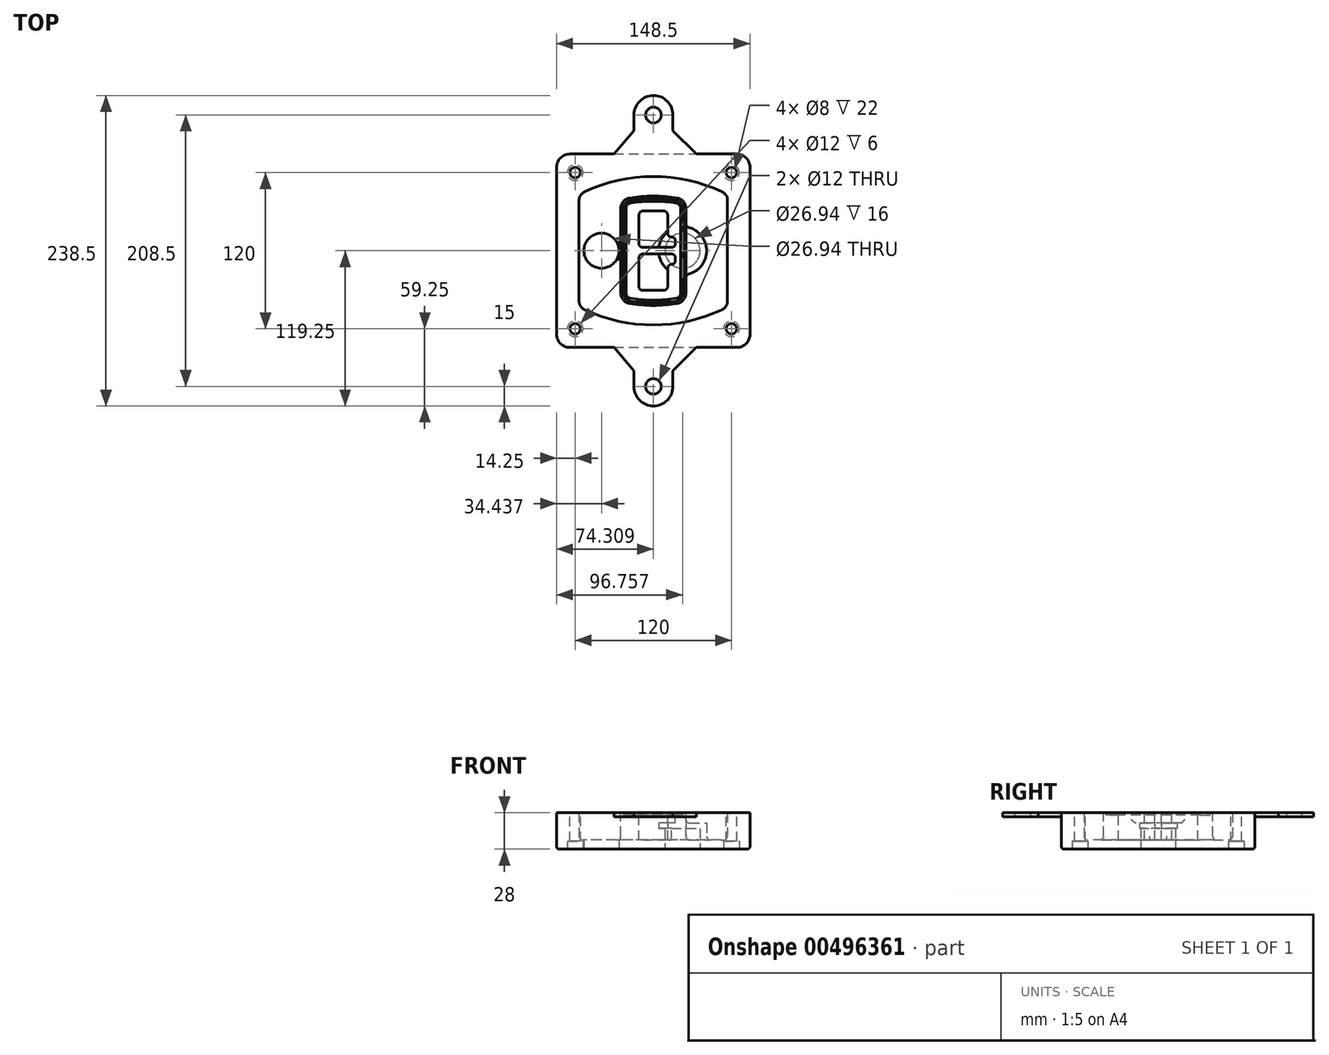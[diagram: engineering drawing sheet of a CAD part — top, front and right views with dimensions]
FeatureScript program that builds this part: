
annotation { "Feature Type Name" : "Feature", "Feature Type Description" : "" }
export const myFeature = defineFeature(function(context is Context, id is Id, definition is map)
    precondition{}
    {
        {
            var Q0;
            Q0=qCreatedBy(makeId("Top.planeOp"),FACE);
            var sketch = newSketch(context, id + "F0", { "sketchPlane" : qUnion([Q0])});
            skPoint(sketch, "E0.rect.middle", {"position": v(0, 0) * mm});
            skLineSegment(sketch, "E1.bottom", {"start": v(-64.25, -74.25) * mm, "end": v(64.25, -74.25) * mm});
            skLineSegment(sketch, "E1.top", {"start": v(-64.25, 74.25) * mm, "end": v(64.25, 74.25) * mm});
            skLineSegment(sketch, "E1.left", {"start": v(-74.25, -64.25) * mm, "end": v(-74.25, 64.25) * mm});
            skLineSegment(sketch, "E1.right", {"start": v(74.25, -64.25) * mm, "end": v(74.25, 64.25) * mm});
            skLineSegment(sketch, "E2", {"start": v(-74.25, 74.25) * mm, "end": v(74.25, -74.25) * mm, "construction": true});
            skLineSegment(sketch, "E3", {"start": v(74.25, 74.25) * mm, "end": v(-74.25, -74.25) * mm, "construction": true});
            skCircle(sketch, "E4", {"center": v(-60, 60) * mm, "radius": 4 * mm});
            skCircle(sketch, "E5", {"center": v(60, 60) * mm, "radius": 4 * mm});
            skCircle(sketch, "E6", {"center": v(60, -60) * mm, "radius": 4 * mm});
            skCircle(sketch, "E7", {"center": v(-60, -60) * mm, "radius": 4 * mm});
            skLineSegment(sketch, "E8", {"start": v(-60, 60) * mm, "end": v(60, 60) * mm, "construction": true});
            skLineSegment(sketch, "E9", {"start": v(60, 60) * mm, "end": v(60, -60) * mm, "construction": true});
            skLineSegment(sketch, "E10", {"start": v(60, -60) * mm, "end": v(-60, -60) * mm, "construction": true});
            skLineSegment(sketch, "E11", {"start": v(-60, -60) * mm, "end": v(-60, 60) * mm, "construction": true});
            skLineSegment(sketch, "E12", {"start": v(-60, 38.83) * mm, "end": v(-60, -38.83) * mm});
            skLineSegment(sketch, "E13", {"start": v(60, 38.83) * mm, "end": v(60, -38.83) * mm});
            skArc(sketch, "E14", {"start": v(54.26, 47.88) * mm, "mid": v(0, 60) * mm, "end": v(-54.26, 47.88) * mm});
            skArc(sketch, "E15", {"start": v(-54.26, -47.88) * mm, "mid": v(0, -60) * mm, "end": v(54.26, -47.88) * mm});
            skLineSegment(sketch, "E16", {"start": v(-60, 0) * mm, "end": v(60, 0) * mm, "construction": true});
            skPoint(sketch, "E17.visualSharp", {"position": v(-60, -45) * mm});
            skArc(sketch, "E17.filletArc", {"start": v(-60, -38.83) * mm, "mid": v(-58.44, -44.2) * mm, "end": v(-54.26, -47.88) * mm});
            skPoint(sketch, "E18.visualSharp", {"position": v(-60, 45) * mm});
            skArc(sketch, "E18.filletArc", {"start": v(-54.26, 47.88) * mm, "mid": v(-58.44, 44.2) * mm, "end": v(-60, 38.83) * mm});
            skPoint(sketch, "E19.visualSharp", {"position": v(60, 45) * mm});
            skArc(sketch, "E19.filletArc", {"start": v(60, 38.83) * mm, "mid": v(58.44, 44.2) * mm, "end": v(54.26, 47.88) * mm});
            skPoint(sketch, "E20.visualSharp", {"position": v(60, -45) * mm});
            skArc(sketch, "E20.filletArc", {"start": v(54.26, -47.88) * mm, "mid": v(58.44, -44.2) * mm, "end": v(60, -38.83) * mm});
            skPoint(sketch, "E21.visualSharp", {"position": v(-74.25, 74.25) * mm});
            skArc(sketch, "E21.filletArc", {"start": v(-64.25, 74.25) * mm, "mid": v(-71.32, 71.32) * mm, "end": v(-74.25, 64.25) * mm});
            skPoint(sketch, "E22.visualSharp", {"position": v(74.25, 74.25) * mm});
            skArc(sketch, "E22.filletArc", {"start": v(74.25, 64.25) * mm, "mid": v(71.32, 71.32) * mm, "end": v(64.25, 74.25) * mm});
            skPoint(sketch, "E23.visualSharp", {"position": v(74.25, -74.25) * mm});
            skArc(sketch, "E23.filletArc", {"start": v(64.25, -74.25) * mm, "mid": v(71.32, -71.32) * mm, "end": v(74.25, -64.25) * mm});
            skPoint(sketch, "E24.visualSharp", {"position": v(-74.25, -74.25) * mm});
            skArc(sketch, "E24.filletArc", {"start": v(-74.25, -64.25) * mm, "mid": v(-71.32, -71.32) * mm, "end": v(-64.25, -74.25) * mm});
            skArc(sketch, "E25.0", {"start": v(57, 38.83) * mm, "mid": v(55.9, 42.58) * mm, "end": v(52.98, 45.17) * mm});
            skLineSegment(sketch, "E25.1", {"start": v(57, 38.83) * mm, "end": v(57, -38.83) * mm});
            skArc(sketch, "E25.2", {"start": v(52.98, -45.17) * mm, "mid": v(55.9, -42.58) * mm, "end": v(57, -38.83) * mm});
            skArc(sketch, "E25.3", {"start": v(-52.98, -45.17) * mm, "mid": v(0, -57) * mm, "end": v(52.98, -45.17) * mm});
            skArc(sketch, "E25.4", {"start": v(-57, -38.83) * mm, "mid": v(-55.9, -42.58) * mm, "end": v(-52.98, -45.17) * mm});
            skArc(sketch, "E25.5", {"start": v(52.98, 45.17) * mm, "mid": v(0, 57) * mm, "end": v(-52.98, 45.17) * mm});
            skLineSegment(sketch, "E25.6", {"start": v(-57, 38.83) * mm, "end": v(-57, -38.83) * mm});
            skArc(sketch, "E25.7", {"start": v(-52.98, 45.17) * mm, "mid": v(-55.9, 42.58) * mm, "end": v(-57, 38.83) * mm});
            skArc(sketch, "E26.0", {"start": v(-55.96, 51.5) * mm, "mid": v(-61.82, 46.33) * mm, "end": v(-64, 38.83) * mm});
            skArc(sketch, "E26.1", {"start": v(55.96, 51.5) * mm, "mid": v(0, 64) * mm, "end": v(-55.96, 51.5) * mm});
            skArc(sketch, "E26.2", {"start": v(64, 38.83) * mm, "mid": v(61.82, 46.33) * mm, "end": v(55.96, 51.5) * mm});
            skLineSegment(sketch, "E26.3", {"start": v(64, 38.83) * mm, "end": v(64, -38.83) * mm});
            skArc(sketch, "E26.4", {"start": v(55.96, -51.5) * mm, "mid": v(61.82, -46.33) * mm, "end": v(64, -38.83) * mm});
            skLineSegment(sketch, "E26.5", {"start": v(-64, 38.83) * mm, "end": v(-64, -38.83) * mm});
            skArc(sketch, "E26.6", {"start": v(-55.96, -51.5) * mm, "mid": v(0, -64) * mm, "end": v(55.96, -51.5) * mm});
            skArc(sketch, "E26.7", {"start": v(-64, -38.83) * mm, "mid": v(-61.82, -46.33) * mm, "end": v(-55.96, -51.5) * mm});
            skSolve(sketch);
        }
        {
            var Q0;
            Q0=makeQuery(id+"F0.imprint","IMPRINT",FACE,{"disambiguationData":[TD([[makeQuery(id+"F0.imprint","IMPRINT",EDGE,{"derivedFrom":sQuery(id+"F0.wireOp",EDGE,"E1.bottom")}),1.0]])]});
            var Q1;
            Q1=makeQuery(id+"F0.imprint","IMPRINT",FACE,{"disambiguationData":[TD([[makeQuery(id+"F0.imprint","IMPRINT",EDGE,{"derivedFrom":sQuery(id+"F0.wireOp",EDGE,"E12")}),1.0]])]});
            var Q2;
            Q2=makeQuery(id+"F0.imprint","IMPRINT",FACE,{"disambiguationData":[TD([[makeQuery(id+"F0.imprint","IMPRINT",EDGE,{"derivedFrom":sQuery(id+"F0.wireOp",EDGE,"E25.0")}),1.0]])]});
            var Q3;
            Q3=makeQuery(id+"F0.imprint","IMPRINT",FACE,{"disambiguationData":[TD([[makeQuery(id+"F0.imprint","IMPRINT",EDGE,{"derivedFrom":sQuery(id+"F0.wireOp",EDGE,"E12")}),-1.0]])]});
            extrude(context, id + "F1", {"entities" : qUnion([Q0, Q1, Q2, Q3]), "oppositeDirection" : true, "depth" : 25 * mm});
        }
        {
            var Q0;
            Q0=makeQuery(id+"F0.imprint","IMPRINT",FACE,{"disambiguationData":[TD([[makeQuery(id+"F0.imprint","IMPRINT",EDGE,{"derivedFrom":sQuery(id+"F0.wireOp",EDGE,"E12")}),1.0]])]});
            extrude(context, id + "F2", {"entities" : qUnion([Q0]), "operationType" : NewBodyOperationType.ADD, "depth" : 3 * mm});
        }
        {
            var Q0;
            Q0=makeQuery(id+"F0.imprint","IMPRINT",FACE,{"disambiguationData":[TD([[makeQuery(id+"F0.imprint","IMPRINT",EDGE,{"derivedFrom":sQuery(id+"F0.wireOp",EDGE,"E25.0")}),1.0]])]});
            extrude(context, id + "F3", {"entities" : qUnion([Q0]), "operationType" : NewBodyOperationType.REMOVE, "oppositeDirection" : true, "depth" : 18 * mm});
        }
        {
            var Q0;
            Q0=makeQuery(id+"F2.opExtrude","CAP_FACE",FACE,{"disambiguationData":[OSD([sQuery(id+"F0.wireOp",EDGE,"E12"),sQuery(id+"F0.wireOp",EDGE,"E13"),sQuery(id+"F0.wireOp",EDGE,"E14"),sQuery(id+"F0.wireOp",EDGE,"E15"),sQuery(id+"F0.wireOp",EDGE,"E17.filletArc"),sQuery(id+"F0.wireOp",EDGE,"E18.filletArc"),sQuery(id+"F0.wireOp",EDGE,"E19.filletArc"),sQuery(id+"F0.wireOp",EDGE,"E20.filletArc"),sQuery(id+"F0.wireOp",EDGE,"E25.0"),sQuery(id+"F0.wireOp",EDGE,"E25.1"),sQuery(id+"F0.wireOp",EDGE,"E25.2"),sQuery(id+"F0.wireOp",EDGE,"E25.3"),sQuery(id+"F0.wireOp",EDGE,"E25.4"),sQuery(id+"F0.wireOp",EDGE,"E25.5"),sQuery(id+"F0.wireOp",EDGE,"E25.6"),sQuery(id+"F0.wireOp",EDGE,"E25.7")])],"isStart":false});
            var sketch = newSketch(context, id + "F4", { "sketchPlane" : qUnion([Q0])});
            skArc(sketch, "E27.0", {"start": v(-18.34, -40.45) * mm, "mid": v(0, -42) * mm, "end": v(18.34, -40.45) * mm});
            skArc(sketch, "E28.0", {"start": v(18.34, 40.45) * mm, "mid": v(0, 42) * mm, "end": v(-18.34, 40.45) * mm});
            skLineSegment(sketch, "E29", {"start": v(-25, 32.57) * mm, "end": v(-25, -32.57) * mm});
            skLineSegment(sketch, "E30", {"start": v(25, 32.57) * mm, "end": v(25, -32.57) * mm});
            skLineSegment(sketch, "E31", {"start": v(-25, 39.1) * mm, "end": v(25, 39.1) * mm, "construction": true});
            skLineSegment(sketch, "E32", {"start": v(-25, -39.1) * mm, "end": v(25, -39.1) * mm, "construction": true});
            skPoint(sketch, "E33.visualSharp", {"position": v(-25, 39.1) * mm});
            skArc(sketch, "E33.filletArc", {"start": v(-18.34, 40.45) * mm, "mid": v(-23.11, 37.73) * mm, "end": v(-25, 32.57) * mm});
            skPoint(sketch, "E34.visualSharp", {"position": v(25, 39.1) * mm});
            skArc(sketch, "E34.filletArc", {"start": v(25, 32.57) * mm, "mid": v(23.11, 37.73) * mm, "end": v(18.34, 40.45) * mm});
            skPoint(sketch, "E35.visualSharp", {"position": v(25, -39.1) * mm});
            skArc(sketch, "E35.filletArc", {"start": v(18.34, -40.45) * mm, "mid": v(23.11, -37.73) * mm, "end": v(25, -32.57) * mm});
            skPoint(sketch, "E36.visualSharp", {"position": v(-25, -39.1) * mm});
            skArc(sketch, "E36.filletArc", {"start": v(-25, -32.57) * mm, "mid": v(-23.11, -37.73) * mm, "end": v(-18.34, -40.45) * mm});
            skArc(sketch, "E37.0", {"start": v(52.98, 45.17) * mm, "mid": v(0, 57) * mm, "end": v(-52.98, 45.17) * mm});
            skArc(sketch, "E37.1", {"start": v(-52.98, 45.17) * mm, "mid": v(-55.9, 42.58) * mm, "end": v(-57, 38.83) * mm});
            skLineSegment(sketch, "E37.2", {"start": v(-57, 38.83) * mm, "end": v(-57, -38.83) * mm});
            skArc(sketch, "E37.3", {"start": v(-57, -38.83) * mm, "mid": v(-55.9, -42.58) * mm, "end": v(-52.98, -45.17) * mm});
            skArc(sketch, "E37.4", {"start": v(-52.98, -45.17) * mm, "mid": v(0, -57) * mm, "end": v(52.98, -45.17) * mm});
            skArc(sketch, "E37.5", {"start": v(52.98, -45.17) * mm, "mid": v(55.9, -42.58) * mm, "end": v(57, -38.83) * mm});
            skLineSegment(sketch, "E37.6", {"start": v(57, 38.83) * mm, "end": v(57, -38.83) * mm});
            skArc(sketch, "E37.7", {"start": v(57, 38.83) * mm, "mid": v(55.9, 42.58) * mm, "end": v(52.98, 45.17) * mm});
            skLineSegment(sketch, "E38.0", {"start": v(23, 32.57) * mm, "end": v(23, -32.57) * mm});
            skArc(sketch, "E38.1", {"start": v(18, -38.48) * mm, "mid": v(21.58, -36.44) * mm, "end": v(23, -32.57) * mm});
            skArc(sketch, "E38.2", {"start": v(-18, -38.48) * mm, "mid": v(0, -40) * mm, "end": v(18, -38.48) * mm});
            skArc(sketch, "E38.3", {"start": v(-23, -32.57) * mm, "mid": v(-21.58, -36.44) * mm, "end": v(-18, -38.48) * mm});
            skLineSegment(sketch, "E38.4", {"start": v(-23, 32.57) * mm, "end": v(-23, -32.57) * mm});
            skArc(sketch, "E38.5", {"start": v(23, 32.57) * mm, "mid": v(21.58, 36.44) * mm, "end": v(18, 38.48) * mm});
            skArc(sketch, "E38.6", {"start": v(-18, 38.48) * mm, "mid": v(-21.58, 36.44) * mm, "end": v(-23, 32.57) * mm});
            skArc(sketch, "E38.7", {"start": v(18, 38.48) * mm, "mid": v(0, 40) * mm, "end": v(-18, 38.48) * mm});
            skArc(sketch, "E39.0", {"start": v(21, 32.57) * mm, "mid": v(20.06, 35.15) * mm, "end": v(17.67, 36.5) * mm});
            skLineSegment(sketch, "E39.1", {"start": v(21, 32.57) * mm, "end": v(21, -32.57) * mm});
            skArc(sketch, "E39.2", {"start": v(17.67, -36.5) * mm, "mid": v(20.06, -35.15) * mm, "end": v(21, -32.57) * mm});
            skArc(sketch, "E39.3", {"start": v(-17.67, -36.5) * mm, "mid": v(0, -38) * mm, "end": v(17.67, -36.5) * mm});
            skArc(sketch, "E39.4", {"start": v(-21, -32.57) * mm, "mid": v(-20.06, -35.15) * mm, "end": v(-17.67, -36.5) * mm});
            skArc(sketch, "E39.5", {"start": v(17.67, 36.5) * mm, "mid": v(0, 38) * mm, "end": v(-17.67, 36.5) * mm});
            skLineSegment(sketch, "E39.6", {"start": v(-21, 32.57) * mm, "end": v(-21, -32.57) * mm});
            skArc(sketch, "E39.7", {"start": v(-17.67, 36.5) * mm, "mid": v(-20.06, 35.15) * mm, "end": v(-21, 32.57) * mm});
            skLineSegment(sketch, "E40", {"start": v(-25, 0) * mm, "end": v(25, 0) * mm, "construction": true});
            skLineSegment(sketch, "E41", {"start": v(-11, 5.5) * mm, "end": v(-11, 27.5) * mm});
            skLineSegment(sketch, "E42", {"start": v(-8, 30.5) * mm, "end": v(8, 30.5) * mm});
            skLineSegment(sketch, "E43", {"start": v(11, 27.5) * mm, "end": v(11, 13.5) * mm});
            skLineSegment(sketch, "E44", {"start": v(14, 10.5) * mm, "end": v(14, 10.5) * mm});
            skLineSegment(sketch, "E45", {"start": v(17, 7.5) * mm, "end": v(17, 5.5) * mm});
            skLineSegment(sketch, "E46", {"start": v(14, 2.5) * mm, "end": v(-8, 2.5) * mm});
            skPoint(sketch, "E47.visualSharp", {"position": v(-11, 30.5) * mm});
            skArc(sketch, "E47.filletArc", {"start": v(-8, 30.5) * mm, "mid": v(-10.12, 29.62) * mm, "end": v(-11, 27.5) * mm});
            skPoint(sketch, "E48.visualSharp", {"position": v(11, 30.5) * mm});
            skArc(sketch, "E48.filletArc", {"start": v(11, 27.5) * mm, "mid": v(10.12, 29.62) * mm, "end": v(8, 30.5) * mm});
            skPoint(sketch, "E49.visualSharp", {"position": v(11, 10.5) * mm});
            skArc(sketch, "E49.filletArc", {"start": v(11, 13.5) * mm, "mid": v(11.88, 11.38) * mm, "end": v(14, 10.5) * mm});
            skPoint(sketch, "E50.visualSharp", {"position": v(17, 10.5) * mm});
            skArc(sketch, "E50.filletArc", {"start": v(17, 7.5) * mm, "mid": v(16.12, 9.62) * mm, "end": v(14, 10.5) * mm});
            skPoint(sketch, "E51.visualSharp", {"position": v(17, 2.5) * mm});
            skArc(sketch, "E51.filletArc", {"start": v(14, 2.5) * mm, "mid": v(16.12, 3.38) * mm, "end": v(17, 5.5) * mm});
            skPoint(sketch, "E52.visualSharp", {"position": v(-11, 2.5) * mm});
            skArc(sketch, "E52.filletArc", {"start": v(-11, 5.5) * mm, "mid": v(-10.12, 3.38) * mm, "end": v(-8, 2.5) * mm});
            skLineSegment(sketch, "E53.0.MirrorCS", {"start": v(14, -2.5) * mm, "end": v(-8, -2.5) * mm});
            skArc(sketch, "E54.0.MirrorCS", {"start": v(-11, -5.5) * mm, "mid": v(-10.12, -3.38) * mm, "end": v(-8, -2.5) * mm});
            skLineSegment(sketch, "E55.0.MirrorCS", {"start": v(-11, -5.5) * mm, "end": v(-11, -27.5) * mm});
            skArc(sketch, "E56.0.MirrorCS", {"start": v(-8, -30.5) * mm, "mid": v(-10.12, -29.62) * mm, "end": v(-11, -27.5) * mm});
            skLineSegment(sketch, "E57.0.MirrorCS", {"start": v(-8, -30.5) * mm, "end": v(8, -30.5) * mm});
            skArc(sketch, "E58.0.MirrorCS", {"start": v(11, -27.5) * mm, "mid": v(10.12, -29.62) * mm, "end": v(8, -30.5) * mm});
            skLineSegment(sketch, "E59.0.MirrorCS", {"start": v(11, -27.5) * mm, "end": v(11, -13.5) * mm});
            skArc(sketch, "E60.0.MirrorCS", {"start": v(11, -13.5) * mm, "mid": v(11.88, -11.38) * mm, "end": v(14, -10.5) * mm});
            skArc(sketch, "E61.0.MirrorCS", {"start": v(17, -7.5) * mm, "mid": v(16.12, -9.62) * mm, "end": v(14, -10.5) * mm});
            skLineSegment(sketch, "E62.0.MirrorCS", {"start": v(17, -7.5) * mm, "end": v(17, -5.5) * mm});
            skArc(sketch, "E63.0.MirrorCS", {"start": v(14, -2.5) * mm, "mid": v(16.12, -3.38) * mm, "end": v(17, -5.5) * mm});
            skSolve(sketch);
        }
        {
            var Q0;
            Q0=makeQuery(id+"F4.imprint","IMPRINT",FACE,{"disambiguationData":[TD([[makeQuery(id+"F4.imprint","IMPRINT",EDGE,{"derivedFrom":sQuery(id+"F4.wireOp",EDGE,"E27.0")}),1.0]])]});
            var Q1;
            Q1=makeQuery(id+"F4.imprint","IMPRINT",FACE,{"disambiguationData":[TD([[makeQuery(id+"F4.imprint","IMPRINT",EDGE,{"derivedFrom":sQuery(id+"F4.wireOp",EDGE,"E38.0")}),-1.0]])]});
            var Q2;
            Q2=makeQuery(id+"F4.imprint","IMPRINT",FACE,{"disambiguationData":[TD([[makeQuery(id+"F4.imprint","IMPRINT",EDGE,{"derivedFrom":sQuery(id+"F4.wireOp",EDGE,"E39.0")}),1.0]])]});
            extrude(context, id + "F5", {"entities" : qUnion([Q0, Q1, Q2]), "operationType" : NewBodyOperationType.ADD, "endBound" : BoundingType.UP_TO_NEXT, "oppositeDirection" : true, "depth" : 25 * mm});
        }
        {
            var Q0;
            Q0=makeQuery(id+"F4.imprint","IMPRINT",FACE,{"disambiguationData":[TD([[makeQuery(id+"F4.imprint","IMPRINT",EDGE,{"derivedFrom":sQuery(id+"F4.wireOp",EDGE,"E38.0")}),-1.0]])]});
            extrude(context, id + "F6", {"entities" : qUnion([Q0]), "operationType" : NewBodyOperationType.REMOVE, "oppositeDirection" : true, "depth" : 2 * mm});
        }
        {
            var Q0;
            Q0=makeQuery(id+"F1.opExtrude","CAP_FACE",FACE,{"disambiguationData":[OSD([sQuery(id+"F0.wireOp",EDGE,"E1.bottom"),sQuery(id+"F0.wireOp",EDGE,"E1.top"),sQuery(id+"F0.wireOp",EDGE,"E1.left"),sQuery(id+"F0.wireOp",EDGE,"E1.right"),sQuery(id+"F0.wireOp",EDGE,"E4"),sQuery(id+"F0.wireOp",EDGE,"E5"),sQuery(id+"F0.wireOp",EDGE,"E6"),sQuery(id+"F0.wireOp",EDGE,"E7"),sQuery(id+"F0.wireOp",EDGE,"E21.filletArc"),sQuery(id+"F0.wireOp",EDGE,"E22.filletArc"),sQuery(id+"F0.wireOp",EDGE,"E23.filletArc"),sQuery(id+"F0.wireOp",EDGE,"E24.filletArc")])],"isStart":false});
            var sketch = newSketch(context, id + "F7", { "sketchPlane" : qUnion([Q0])});
            skCircle(sketch, "E64", {"center": v(22.5, 0) * mm, "radius": 13.47 * mm});
            skCircle(sketch, "E65", {"center": v(-39.81, 0) * mm, "radius": 13.47 * mm});
            skLineSegment(sketch, "E66", {"start": v(74.25, 0) * mm, "end": v(-74.25, 0) * mm});
            skCircle(sketch, "E67", {"center": v(22.5, 0) * mm, "radius": 18.47 * mm});
            skCircle(sketch, "E68", {"center": v(60, -60) * mm, "radius": 6 * mm});
            skCircle(sketch, "E69", {"center": v(-60, -60) * mm, "radius": 6 * mm});
            skCircle(sketch, "E70", {"center": v(-60, 60) * mm, "radius": 6 * mm});
            skCircle(sketch, "E71", {"center": v(60, 60) * mm, "radius": 6 * mm});
            skSolve(sketch);
        }
        {
            var Q0;
            {var subQ1=sQuery(id+"F7.wireOp",EDGE,"E66");var subQ4=sQuery(id+"F7.wireOp",EDGE,"E64");var subQ6=makeQuery(id+"F7.imprint","INTERSECT",VERTEX,{"disambiguationData":[OD(0.0)],"derivedFrom":[subQ4,subQ1]});Q0=makeQuery(id+"F7.imprint","IMPRINT",FACE,{"disambiguationData":[TD([[makeQuery(id+"F7.imprint","IMPRINT",EDGE,{"disambiguationData":[TD([[subQ6,-1.0]])],"derivedFrom":subQ4}),-1.0]])]});}
            var Q1;
            {var subQ0=sQuery(id+"F7.wireOp",EDGE,"E66");var subQ1=sQuery(id+"F7.wireOp",EDGE,"E64");var subQ3=makeQuery(id+"F7.imprint","INTERSECT",VERTEX,{"disambiguationData":[OD(0.0)],"derivedFrom":[subQ1,subQ0]});Q1=makeQuery(id+"F7.imprint","IMPRINT",FACE,{"disambiguationData":[TD([[makeQuery(id+"F7.imprint","IMPRINT",EDGE,{"disambiguationData":[TD([[subQ3,-1.0]])],"derivedFrom":subQ1}),1.0]])]});}
            var Q2;
            {var subQ0=sQuery(id+"F7.wireOp",EDGE,"E66");var subQ1=sQuery(id+"F7.wireOp",EDGE,"E64");var subQ3=makeQuery(id+"F7.imprint","INTERSECT",VERTEX,{"disambiguationData":[OD(0.0)],"derivedFrom":[subQ1,subQ0]});Q2=makeQuery(id+"F7.imprint","IMPRINT",FACE,{"disambiguationData":[TD([[makeQuery(id+"F7.imprint","IMPRINT",EDGE,{"disambiguationData":[TD([[subQ3,1.0]])],"derivedFrom":subQ1}),1.0]])]});}
            var Q3;
            {var subQ1=sQuery(id+"F7.wireOp",EDGE,"E66");var subQ4=sQuery(id+"F7.wireOp",EDGE,"E64");var subQ6=makeQuery(id+"F7.imprint","INTERSECT",VERTEX,{"disambiguationData":[OD(0.0)],"derivedFrom":[subQ4,subQ1]});Q3=makeQuery(id+"F7.imprint","IMPRINT",FACE,{"disambiguationData":[TD([[makeQuery(id+"F7.imprint","IMPRINT",EDGE,{"disambiguationData":[TD([[subQ6,1.0]])],"derivedFrom":subQ4}),-1.0]])]});}
            extrude(context, id + "F8", {"entities" : qUnion([Q0, Q1, Q2, Q3]), "operationType" : NewBodyOperationType.ADD, "oppositeDirection" : true, "depth" : 20 * mm});
        }
        {
            var Q0;
            {var subQ0=sQuery(id+"F7.wireOp",EDGE,"E66");var subQ1=sQuery(id+"F7.wireOp",EDGE,"E64");var subQ3=makeQuery(id+"F7.imprint","INTERSECT",VERTEX,{"disambiguationData":[OD(0.0)],"derivedFrom":[subQ1,subQ0]});Q0=makeQuery(id+"F7.imprint","IMPRINT",FACE,{"disambiguationData":[TD([[makeQuery(id+"F7.imprint","IMPRINT",EDGE,{"disambiguationData":[TD([[subQ3,-1.0]])],"derivedFrom":subQ1}),1.0]])]});}
            var Q1;
            {var subQ0=sQuery(id+"F7.wireOp",EDGE,"E66");var subQ1=sQuery(id+"F7.wireOp",EDGE,"E64");var subQ3=makeQuery(id+"F7.imprint","INTERSECT",VERTEX,{"disambiguationData":[OD(0.0)],"derivedFrom":[subQ1,subQ0]});Q1=makeQuery(id+"F7.imprint","IMPRINT",FACE,{"disambiguationData":[TD([[makeQuery(id+"F7.imprint","IMPRINT",EDGE,{"disambiguationData":[TD([[subQ3,1.0]])],"derivedFrom":subQ1}),1.0]])]});}
            extrude(context, id + "F9", {"entities" : qUnion([Q0, Q1]), "operationType" : NewBodyOperationType.REMOVE, "oppositeDirection" : true, "depth" : 16 * mm});
        }
        {
            var Q0;
            {var subQ0=sQuery(id+"F7.wireOp",EDGE,"E66");var subQ1=sQuery(id+"F7.wireOp",EDGE,"E65");var subQ3=makeQuery(id+"F7.imprint","INTERSECT",VERTEX,{"disambiguationData":[OD(0.0)],"derivedFrom":[subQ1,subQ0]});Q0=makeQuery(id+"F7.imprint","IMPRINT",FACE,{"disambiguationData":[TD([[makeQuery(id+"F7.imprint","IMPRINT",EDGE,{"disambiguationData":[TD([[subQ3,-1.0]])],"derivedFrom":subQ1}),1.0]])]});}
            var Q1;
            {var subQ0=sQuery(id+"F7.wireOp",EDGE,"E66");var subQ1=sQuery(id+"F7.wireOp",EDGE,"E65");var subQ3=makeQuery(id+"F7.imprint","INTERSECT",VERTEX,{"disambiguationData":[OD(0.0)],"derivedFrom":[subQ1,subQ0]});Q1=makeQuery(id+"F7.imprint","IMPRINT",FACE,{"disambiguationData":[TD([[makeQuery(id+"F7.imprint","IMPRINT",EDGE,{"disambiguationData":[TD([[subQ3,1.0]])],"derivedFrom":subQ1}),1.0]])]});}
            extrude(context, id + "F10", {"entities" : qUnion([Q0, Q1]), "operationType" : NewBodyOperationType.REMOVE, "oppositeDirection" : true, "depth" : 25 * mm});
        }
        {
            var Q0;
            Q0=makeQuery(id+"F7.imprint","IMPRINT",FACE,{"disambiguationData":[TD([[makeQuery(id+"F7.imprint","IMPRINT",EDGE,{"derivedFrom":sQuery(id+"F7.wireOp",EDGE,"E68")}),1.0]])]});
            var Q1;
            Q1=makeQuery(id+"F7.imprint","IMPRINT",FACE,{"disambiguationData":[TD([[makeQuery(id+"F7.imprint","IMPRINT",EDGE,{"derivedFrom":makeQuery(id+"F1.opExtrude","CAP_EDGE",EDGE,{"disambiguationData":[OSD([sQuery(id+"F0.wireOp",EDGE,"E5")])],"isStart":false})}),-1.0]])]});
            var Q2;
            Q2=makeQuery(id+"F7.imprint","IMPRINT",FACE,{"disambiguationData":[TD([[makeQuery(id+"F7.imprint","IMPRINT",EDGE,{"derivedFrom":sQuery(id+"F7.wireOp",EDGE,"E69")}),1.0]])]});
            var Q3;
            Q3=makeQuery(id+"F7.imprint","IMPRINT",FACE,{"disambiguationData":[TD([[makeQuery(id+"F7.imprint","IMPRINT",EDGE,{"derivedFrom":makeQuery(id+"F1.opExtrude","CAP_EDGE",EDGE,{"disambiguationData":[OSD([sQuery(id+"F0.wireOp",EDGE,"E4")])],"isStart":false})}),-1.0]])]});
            var Q4;
            Q4=makeQuery(id+"F7.imprint","IMPRINT",FACE,{"disambiguationData":[TD([[makeQuery(id+"F7.imprint","IMPRINT",EDGE,{"derivedFrom":sQuery(id+"F7.wireOp",EDGE,"E70")}),1.0]])]});
            var Q5;
            Q5=makeQuery(id+"F7.imprint","IMPRINT",FACE,{"disambiguationData":[TD([[makeQuery(id+"F7.imprint","IMPRINT",EDGE,{"derivedFrom":makeQuery(id+"F1.opExtrude","CAP_EDGE",EDGE,{"disambiguationData":[OSD([sQuery(id+"F0.wireOp",EDGE,"E7")])],"isStart":false})}),-1.0]])]});
            var Q6;
            Q6=makeQuery(id+"F7.imprint","IMPRINT",FACE,{"disambiguationData":[TD([[makeQuery(id+"F7.imprint","IMPRINT",EDGE,{"derivedFrom":sQuery(id+"F7.wireOp",EDGE,"E71")}),1.0]])]});
            var Q7;
            Q7=makeQuery(id+"F7.imprint","IMPRINT",FACE,{"disambiguationData":[TD([[makeQuery(id+"F7.imprint","IMPRINT",EDGE,{"derivedFrom":makeQuery(id+"F1.opExtrude","CAP_EDGE",EDGE,{"disambiguationData":[OSD([sQuery(id+"F0.wireOp",EDGE,"E6")])],"isStart":false})}),-1.0]])]});
            extrude(context, id + "F11", {"entities" : qUnion([Q0, Q1, Q2, Q3, Q4, Q5, Q6, Q7]), "operationType" : NewBodyOperationType.REMOVE, "oppositeDirection" : true, "depth" : 6 * mm});
        }
        {
            var Q0;
            Q0=makeQuery(id+"F9.boolean.opBoolean","COPY",FACE,{"derivedFrom":makeQuery(id+"F9.opExtrude","CAP_FACE",FACE,{"disambiguationData":[OSD([sQuery(id+"F7.wireOp",EDGE,"E64")])],"isStart":false})});
            var sketch = newSketch(context, id + "F12", { "sketchPlane" : qUnion([Q0])});
            skArc(sketch, "E72.0", {"start": v(11, 14.45) * mm, "mid": v(6.45, 9.13) * mm, "end": v(4.2, 2.5) * mm});
            skArc(sketch, "E72.1", {"start": v(4.2, -2.5) * mm, "mid": v(6.45, -9.13) * mm, "end": v(11, -14.45) * mm});
            skLineSegment(sketch, "E73", {"start": v(4.2, -2.5) * mm, "end": v(14, -2.5) * mm});
            skLineSegment(sketch, "E74.0", {"start": v(14, 2.5) * mm, "end": v(4.2, 2.5) * mm});
            skArc(sketch, "E74.1", {"start": v(14, 2.5) * mm, "mid": v(16.12, 3.38) * mm, "end": v(17, 5.5) * mm});
            skLineSegment(sketch, "E74.2", {"start": v(17, 7.5) * mm, "end": v(17, 5.5) * mm});
            skArc(sketch, "E74.3", {"start": v(17, 7.5) * mm, "mid": v(16.12, 9.62) * mm, "end": v(14, 10.5) * mm});
            skArc(sketch, "E74.4", {"start": v(11, 13.5) * mm, "mid": v(11.88, 11.38) * mm, "end": v(14, 10.5) * mm});
            skLineSegment(sketch, "E74.5", {"start": v(11, 14.45) * mm, "end": v(11, 13.5) * mm});
            skLineSegment(sketch, "E74.7", {"start": v(14, -2.5) * mm, "end": v(4.2, -2.5) * mm});
            skArc(sketch, "E74.8", {"start": v(14, -2.5) * mm, "mid": v(16.12, -3.38) * mm, "end": v(17, -5.5) * mm});
            skLineSegment(sketch, "E74.9", {"start": v(17, -7.5) * mm, "end": v(17, -5.5) * mm});
            skArc(sketch, "E74.10", {"start": v(17, -7.5) * mm, "mid": v(16.12, -9.62) * mm, "end": v(14, -10.5) * mm});
            skArc(sketch, "E74.11", {"start": v(11, -13.5) * mm, "mid": v(11.88, -11.38) * mm, "end": v(14, -10.5) * mm});
            skLineSegment(sketch, "E74.12", {"start": v(11, -14.45) * mm, "end": v(11, -13.5) * mm});
            skPoint(sketch, "E75.orphan", {"position": v(11, -27.5) * mm});
            skPoint(sketch, "E76.orphan", {"position": v(-8, -2.5) * mm});
            skPoint(sketch, "E77.orphan", {"position": v(-8, 2.5) * mm});
            skPoint(sketch, "E78.orphan", {"position": v(11, 27.5) * mm});
            skSolve(sketch);
        }
        {
            var Q0;
            {var subQ7=sQuery(id+"F12.wireOp",EDGE,"E72.0");var subQ14=sQuery(id+"F12.wireOp",EDGE,"E72.1");var subQ16=sQuery(id+"F12.wireOp",EDGE,"E74.1");var subQ18=sQuery(id+"F12.wireOp",EDGE,"E74.8");Q0=qUnion([makeQuery(id+"F12.imprint","IMPRINT",FACE,{"disambiguationData":[TD([[makeQuery(id+"F12.imprint","IMPRINT",EDGE,{"derivedFrom":subQ7}),1.0]])]}),makeQuery(id+"F12.imprint","IMPRINT",FACE,{"disambiguationData":[TD([[makeQuery(id+"F12.imprint","IMPRINT",EDGE,{"derivedFrom":subQ14}),1.0]])]}),makeQuery(id+"F12.imprint","IMPRINT",FACE,{"disambiguationData":[TD([[makeQuery(id+"F12.imprint","IMPRINT",EDGE,{"derivedFrom":subQ16}),1.0]])]}),makeQuery(id+"F12.imprint","IMPRINT",FACE,{"disambiguationData":[TD([[makeQuery(id+"F12.imprint","IMPRINT",EDGE,{"derivedFrom":subQ18}),-1.0]])]})]);}
            var Q1;
            Q1=makeQuery(id+"F5.boolean.opBoolean","SPLIT",FACE,{"disambiguationData":[TD([makeQuery(id+"F5.opExtrude","SWEPT_FACE",FACE,{"disambiguationData":[OSD([sQuery(id+"F4.wireOp",EDGE,"E41")])]})])],"derivedFrom":makeQuery(id+"F3.boolean.opBoolean","COPY",FACE,{"derivedFrom":makeQuery(id+"F3.opExtrude","CAP_FACE",FACE,{"disambiguationData":[OSD([sQuery(id+"F0.wireOp",EDGE,"E25.0"),sQuery(id+"F0.wireOp",EDGE,"E25.1"),sQuery(id+"F0.wireOp",EDGE,"E25.2"),sQuery(id+"F0.wireOp",EDGE,"E25.3"),sQuery(id+"F0.wireOp",EDGE,"E25.4"),sQuery(id+"F0.wireOp",EDGE,"E25.5"),sQuery(id+"F0.wireOp",EDGE,"E25.6"),sQuery(id+"F0.wireOp",EDGE,"E25.7")])],"isStart":false})})});
            extrude(context, id + "F13", {"entities" : qUnion([Q0]), "operationType" : NewBodyOperationType.REMOVE, "endBound" : BoundingType.UP_TO_SURFACE, "endBoundEntityFace" : qUnion([Q1]), "depth" : 25 * mm});
        }
        {
            var Q0;
            Q0=makeQuery(id+"F3.boolean.opBoolean","COPY",EDGE,{"derivedFrom":makeQuery(id+"F3.opExtrude","CAP_EDGE",EDGE,{"disambiguationData":[OSD([sQuery(id+"F0.wireOp",EDGE,"E25.6")])],"isStart":false})});
            var Q1;
            Q1=makeQuery(id+"F8.boolean.opBoolean","INTERSECT",EDGE,{"derivedFrom":[makeQuery(id+"F5.opExtrude","SWEPT_FACE",FACE,{"disambiguationData":[OSD([sQuery(id+"F4.wireOp",EDGE,"E30")])]}),makeQuery(id+"F8.opExtrude","CAP_FACE",FACE,{"disambiguationData":[OSD([sQuery(id+"F7.wireOp",EDGE,"E67")])],"isStart":false})]});
            var Q2;
            Q2=makeQuery(id+"F8.boolean.opBoolean","INTERSECT",EDGE,{"disambiguationData":[OD(1.0)],"derivedFrom":[makeQuery(id+"F5.opExtrude","SWEPT_FACE",FACE,{"disambiguationData":[OSD([sQuery(id+"F4.wireOp",EDGE,"E30")])]}),makeQuery(id+"F8.opExtrude","SWEPT_FACE",FACE,{"disambiguationData":[OSD([sQuery(id+"F7.wireOp",EDGE,"E67")])]})]});
            var Q3;
            {var subQ0=sQuery(id+"F4.wireOp",EDGE,"E30");Q3=makeQuery(id+"F8.boolean.opBoolean","SPLIT",EDGE,{"disambiguationData":[TD([makeQuery(id+"F5.opExtrude","SWEPT_FACE",FACE,{"disambiguationData":[OSD([sQuery(id+"F4.wireOp",EDGE,"E35.filletArc")])]})])],"derivedFrom":makeQuery(id+"F5.opExtrude","CAP_EDGE",EDGE,{"disambiguationData":[OSD([subQ0])],"isStart":false})});}
            var Q4;
            {var subQ0=sQuery(id+"F0.wireOp",EDGE,"E25.7");var subQ1=sQuery(id+"F0.wireOp",EDGE,"E25.1");var subQ2=sQuery(id+"F0.wireOp",EDGE,"E25.6");var subQ3=sQuery(id+"F0.wireOp",EDGE,"E25.5");var subQ4=sQuery(id+"F0.wireOp",EDGE,"E25.4");var subQ5=sQuery(id+"F0.wireOp",EDGE,"E25.0");var subQ6=sQuery(id+"F0.wireOp",EDGE,"E25.2");var subQ7=sQuery(id+"F0.wireOp",EDGE,"E25.3");Q4=makeQuery(id+"F8.boolean.opBoolean","INTERSECT",EDGE,{"derivedFrom":[makeQuery(id+"F5.boolean.opBoolean","SPLIT",FACE,{"disambiguationData":[TD([makeQuery(id+"F2.opExtrude","SWEPT_FACE",FACE,{"disambiguationData":[OSD([subQ5])]})])],"derivedFrom":makeQuery(id+"F3.boolean.opBoolean","COPY",FACE,{"derivedFrom":makeQuery(id+"F3.opExtrude","CAP_FACE",FACE,{"disambiguationData":[OSD([subQ5,subQ1,subQ6,subQ7,subQ4,subQ3,subQ2,subQ0])],"isStart":false})})}),makeQuery(id+"F8.opExtrude","SWEPT_FACE",FACE,{"disambiguationData":[OSD([sQuery(id+"F7.wireOp",EDGE,"E67")])]})]});}
            var Q5;
            Q5=makeQuery(id+"F8.boolean.opBoolean","INTERSECT",EDGE,{"disambiguationData":[OD(0.0)],"derivedFrom":[makeQuery(id+"F5.opExtrude","SWEPT_FACE",FACE,{"disambiguationData":[OSD([sQuery(id+"F4.wireOp",EDGE,"E30")])]}),makeQuery(id+"F8.opExtrude","SWEPT_FACE",FACE,{"disambiguationData":[OSD([sQuery(id+"F7.wireOp",EDGE,"E67")])]})]});
            fillet(context, id + "F14", {"entities" : qUnion([Q0, Q1, Q2, Q3, Q4, Q5]), "radius" : 3 * mm, "tangentPropagation" : true, "allowEdgeOverflow" : false});
        }
        {
            var Q0;
            Q0=makeQuery(id+"F1.opExtrude","CAP_EDGE",EDGE,{"disambiguationData":[OSD([sQuery(id+"F0.wireOp",EDGE,"E1.bottom")])],"isStart":false});
            fillet(context, id + "F15", {"entities" : qUnion([Q0]), "radius" : 2 * mm, "tangentPropagation" : true, "allowEdgeOverflow" : false});
        }
        {
            var Q0;
            {var subQ0=sQuery(id+"F0.wireOp",EDGE,"E21.filletArc");var subQ1=sQuery(id+"F0.wireOp",EDGE,"E7");var subQ2=sQuery(id+"F0.wireOp",EDGE,"E6");var subQ3=sQuery(id+"F0.wireOp",EDGE,"E5");var subQ4=sQuery(id+"F0.wireOp",EDGE,"E4");var subQ5=sQuery(id+"F0.wireOp",EDGE,"E22.filletArc");var subQ6=sQuery(id+"F0.wireOp",EDGE,"E1.bottom");var subQ7=sQuery(id+"F0.wireOp",EDGE,"E1.right");var subQ8=sQuery(id+"F0.wireOp",EDGE,"E1.top");var subQ9=sQuery(id+"F0.wireOp",EDGE,"E1.left");var subQ10=sQuery(id+"F0.wireOp",EDGE,"E23.filletArc");var subQ11=sQuery(id+"F0.wireOp",EDGE,"E24.filletArc");Q0=makeQuery(id+"F2.boolean.opBoolean","SPLIT",FACE,{"disambiguationData":[TD([makeQuery(id+"F1.opExtrude","SWEPT_FACE",FACE,{"disambiguationData":[OSD([subQ6])]})])],"derivedFrom":makeQuery(id+"F1.opExtrude","CAP_FACE",FACE,{"disambiguationData":[OSD([subQ6,subQ8,subQ9,subQ7,subQ4,subQ3,subQ2,subQ1,subQ0,subQ5,subQ10,subQ11])],"isStart":true})});}
            var sketch = newSketch(context, id + "F16", { "sketchPlane" : qUnion([Q0])});
            skLineSegment(sketch, "E79", {"start": v(-30.3, 74.25) * mm, "end": v(-14.94, 92.25) * mm});
            skLineSegment(sketch, "E80", {"start": v(-14.94, 92.25) * mm, "end": v(-14.94, 104.25) * mm});
            skArc(sketch, "E81", {"start": v(15.06, 104.25) * mm, "mid": v(0.06, 119.25) * mm, "end": v(-14.94, 104.25) * mm});
            skCircle(sketch, "E82", {"center": v(0.06, 104.25) * mm, "radius": 6 * mm});
            skLineSegment(sketch, "E83", {"start": v(33.06, 74.25) * mm, "end": v(15.06, 92.25) * mm});
            skLineSegment(sketch, "E84", {"start": v(15.06, 92.25) * mm, "end": v(15.06, 104.25) * mm});
            skLineSegment(sketch, "E85", {"start": v(-74.25, 0) * mm, "end": v(74.25, 0) * mm, "construction": true});
            skLineSegment(sketch, "E86.MirrorCS", {"start": v(33.06, -74.25) * mm, "end": v(15.06, -92.25) * mm});
            skLineSegment(sketch, "E87.MirrorCS", {"start": v(15.06, -92.25) * mm, "end": v(15.06, -104.25) * mm});
            skArc(sketch, "E88.MirrorCS", {"start": v(15.06, -104.25) * mm, "mid": v(0.06, -119.25) * mm, "end": v(-14.94, -104.25) * mm});
            skCircle(sketch, "E89.MirrorC", {"center": v(0.06, -104.25) * mm, "radius": 6 * mm});
            skLineSegment(sketch, "E90.MirrorCS", {"start": v(-14.94, -92.25) * mm, "end": v(-14.94, -104.25) * mm});
            skLineSegment(sketch, "E91.MirrorCS", {"start": v(-30.3, -74.25) * mm, "end": v(-14.94, -92.25) * mm});
            skSolve(sketch);
        }
        {
            var Q0;
            Q0=makeQuery(id+"F16.imprint","IMPRINT",FACE,{"disambiguationData":[TD([[makeQuery(id+"F16.imprint","IMPRINT",EDGE,{"derivedFrom":makeQuery(id+"F1.opExtrude","CAP_EDGE",EDGE,{"disambiguationData":[OSD([sQuery(id+"F0.wireOp",EDGE,"E1.left")])],"isStart":true})}),-1.0]])]});
            var Q1;
            {var subQ0=sQuery(id+"F16.wireOp",EDGE,"E79");Q1=makeQuery(id+"F16.imprint","IMPRINT",FACE,{"disambiguationData":[TD([[makeQuery(id+"F16.imprint","IMPRINT",EDGE,{"derivedFrom":subQ0}),-1.0]])]});}
            var Q2;
            {var subQ0=sQuery(id+"F16.wireOp",EDGE,"E86.MirrorCS");Q2=makeQuery(id+"F16.imprint","IMPRINT",FACE,{"disambiguationData":[TD([[makeQuery(id+"F16.imprint","IMPRINT",EDGE,{"derivedFrom":subQ0}),-1.0]])]});}
            var Q3;
            Q3=makeQuery(id+"F2.opExtrude","CAP_FACE",FACE,{"disambiguationData":[OSD([sQuery(id+"F0.wireOp",EDGE,"E12"),sQuery(id+"F0.wireOp",EDGE,"E13"),sQuery(id+"F0.wireOp",EDGE,"E14"),sQuery(id+"F0.wireOp",EDGE,"E15"),sQuery(id+"F0.wireOp",EDGE,"E17.filletArc"),sQuery(id+"F0.wireOp",EDGE,"E18.filletArc"),sQuery(id+"F0.wireOp",EDGE,"E19.filletArc"),sQuery(id+"F0.wireOp",EDGE,"E20.filletArc"),sQuery(id+"F0.wireOp",EDGE,"E25.0"),sQuery(id+"F0.wireOp",EDGE,"E25.1"),sQuery(id+"F0.wireOp",EDGE,"E25.2"),sQuery(id+"F0.wireOp",EDGE,"E25.3"),sQuery(id+"F0.wireOp",EDGE,"E25.4"),sQuery(id+"F0.wireOp",EDGE,"E25.5"),sQuery(id+"F0.wireOp",EDGE,"E25.6"),sQuery(id+"F0.wireOp",EDGE,"E25.7")])],"isStart":false});
            extrude(context, id + "F17", {"entities" : qUnion([Q0, Q1, Q2]), "operationType" : NewBodyOperationType.ADD, "endBound" : BoundingType.UP_TO_SURFACE, "endBoundEntityFace" : qUnion([Q3]), "depth" : 25 * mm});
        }
    });
